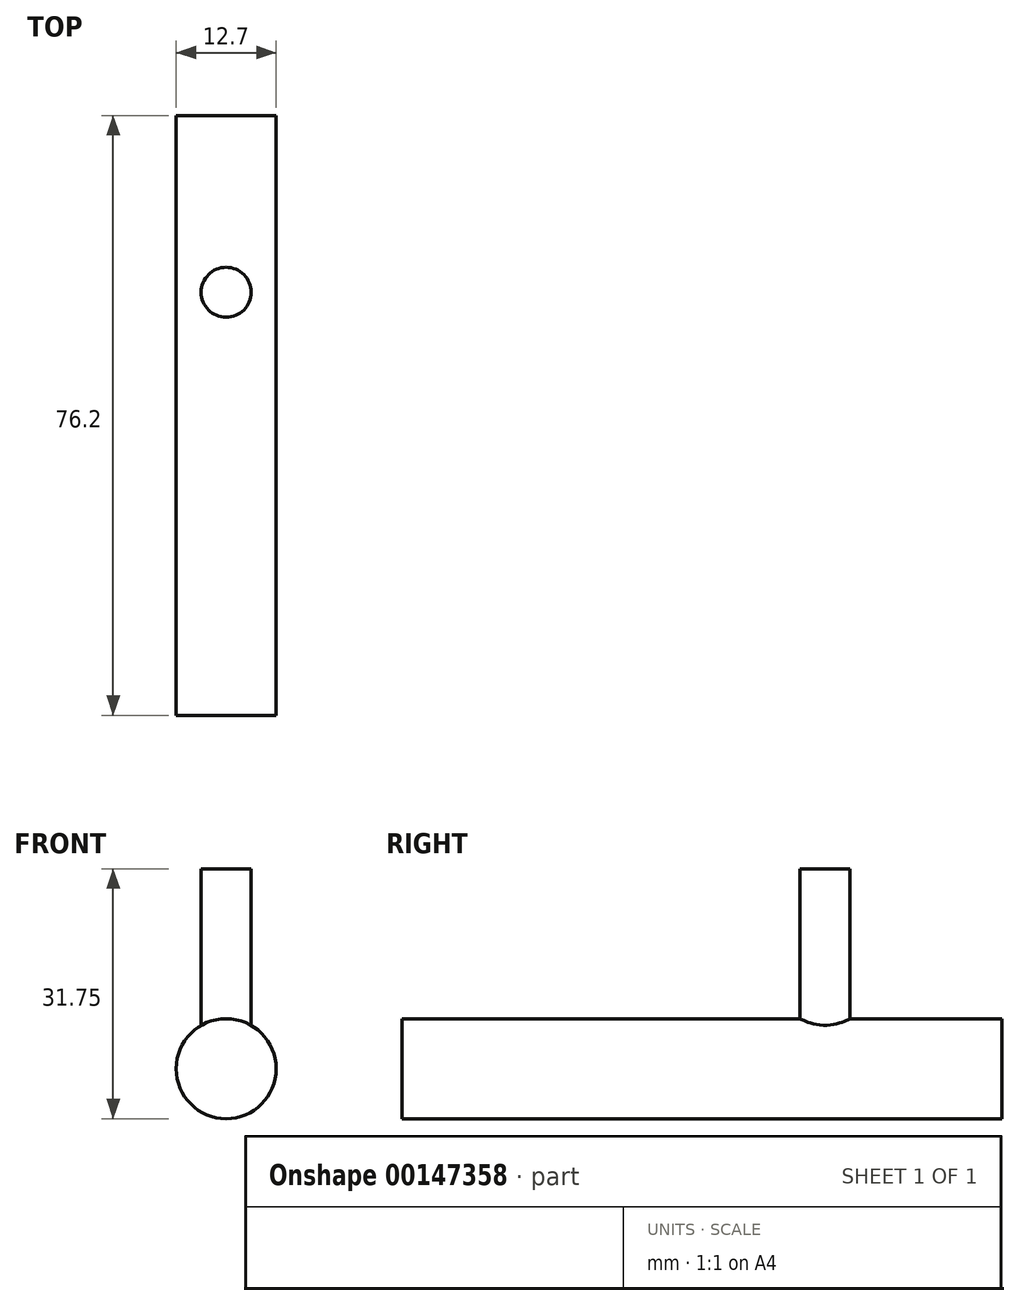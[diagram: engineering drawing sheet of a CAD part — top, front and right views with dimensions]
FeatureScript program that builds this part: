
annotation { "Feature Type Name" : "Feature", "Feature Type Description" : "" }
export const myFeature = defineFeature(function(context is Context, id is Id, definition is map)
    precondition{}
    {
        {
            var Q0;
            Q0=qCreatedBy(makeId("Front.planeOp"),FACE);
            var sketch = newSketch(context, id + "F0", { "sketchPlane" : qUnion([Q0])});
            skCircle(sketch, "E0", {"center": v(0, 0) * mm, "radius": 6.35 * mm});
            skPoint(sketch, "E1", {"position": v(0, 6.35) * mm});
            skLineSegment(sketch, "E2", {"start": v(-3.07, 5.56) * mm, "end": v(-3.07, 31.75) * mm});
            skPoint(sketch, "E3", {"position": v(3.07, 5.56) * mm});
            skLineSegment(sketch, "E4", {"start": v(3.07, 5.56) * mm, "end": v(3.07, 31.75) * mm});
            skLineSegment(sketch, "E5", {"start": v(3.07, 31.75) * mm, "end": v(-3.07, 31.75) * mm});
            skPoint(sketch, "E6", {"position": v(0, 31.75) * mm});
            skSolve(sketch);
        }
        {
            var Q0;
            {var subQ0=sQuery(id+"F0.wireOp",EDGE,"E0");var subQ1=makeQuery(id+"F0.imprint","INTERSECT",VERTEX,{"derivedFrom":[subQ0,sQuery(id+"F0.wireOp",EDGE,"E2")]});Q0=makeQuery(id+"F0.imprint","IMPRINT",FACE,{"disambiguationData":[TD([[makeQuery(id+"F0.imprint","IMPRINT",EDGE,{"disambiguationData":[TD([[subQ1,1.0]])],"derivedFrom":subQ0}),1.0]])]});}
            extrude(context, id + "F1", {"entities" : qUnion([Q0]), "depth" : 76.2 * mm});
        }
        {
            var Q0;
            Q0=qCreatedBy(makeId("Top.planeOp"),FACE);
            var sketch = newSketch(context, id + "F2", { "sketchPlane" : qUnion([Q0])});
            skCircle(sketch, "E7", {"center": v(0, -22.47) * mm, "radius": 3.18 * mm});
            skSolve(sketch);
        }
        {
            var Q0;
            Q0 = qSketchRegion(id + "F2", true);
            extrude(context, id + "F3", {"entities" : qUnion([Q0]), "operationType" : NewBodyOperationType.ADD, "depth" : 25.4 * mm});
        }
    });
